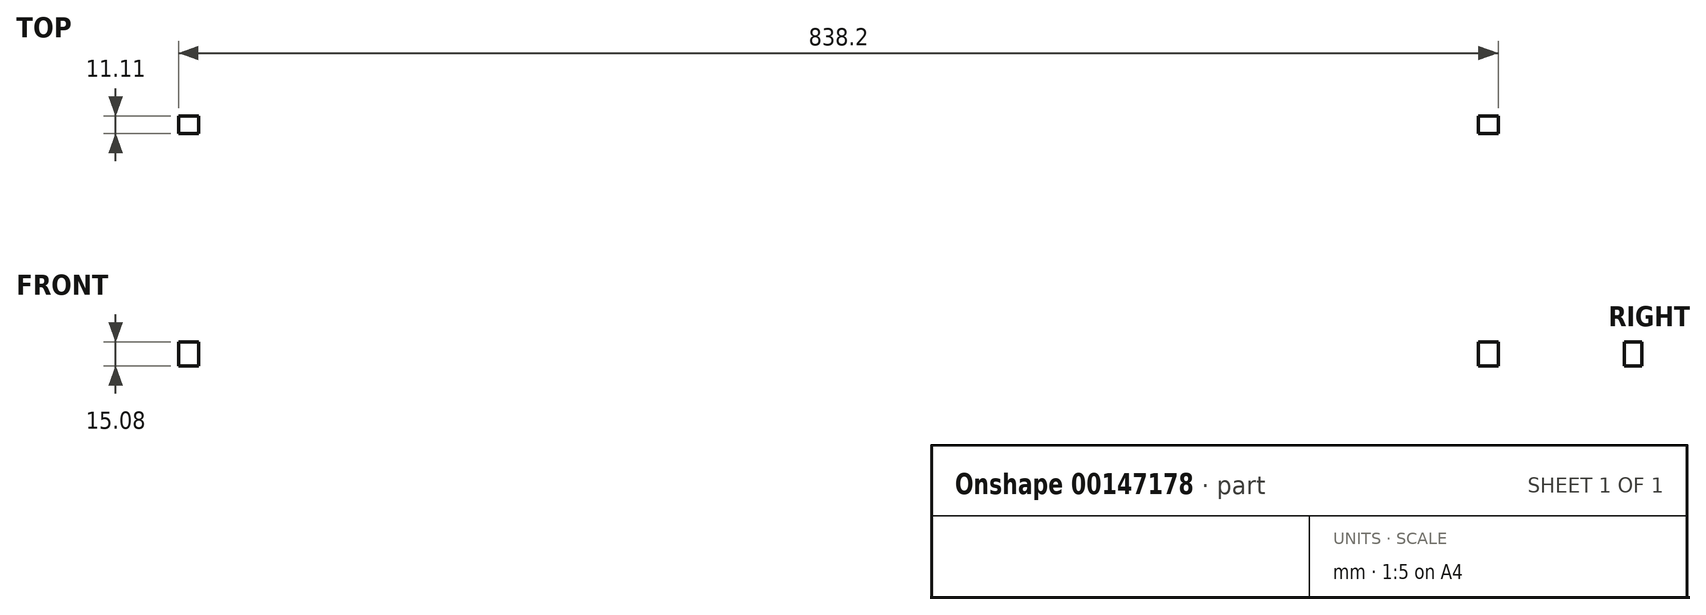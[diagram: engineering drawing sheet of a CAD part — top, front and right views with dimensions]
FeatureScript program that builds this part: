
annotation { "Feature Type Name" : "Feature", "Feature Type Description" : "" }
export const myFeature = defineFeature(function(context is Context, id is Id, definition is map)
    precondition{}
    {
        {
            var Q0;
            Q0=qCreatedBy(makeId("Top.planeOp"),FACE);
            var sketch = newSketch(context, id + "F0", { "sketchPlane" : qUnion([Q0])});
            skLineSegment(sketch, "E0.bottom", {"start": v(0, 0) * mm, "end": v(838.2, 0) * mm});
            skLineSegment(sketch, "E0.top", {"start": v(0, 342.9) * mm, "end": v(838.2, 342.9) * mm});
            skLineSegment(sketch, "E0.left", {"start": v(0, 0) * mm, "end": v(0, 342.9) * mm});
            skLineSegment(sketch, "E0.right", {"start": v(838.2, 0) * mm, "end": v(838.2, 342.9) * mm});
            skLineSegment(sketch, "E1.bottom", {"start": v(0, 0) * mm, "end": v(12.7, 0) * mm});
            skLineSegment(sketch, "E1.top", {"start": v(0, 11.11) * mm, "end": v(12.7, 11.11) * mm});
            skLineSegment(sketch, "E1.left", {"start": v(0, 0) * mm, "end": v(0, 11.11) * mm});
            skLineSegment(sketch, "E1.right", {"start": v(12.7, 0) * mm, "end": v(12.7, 11.11) * mm});
            skLineSegment(sketch, "E2.bottom", {"start": v(12.7, 342.9) * mm, "end": v(0, 342.9) * mm});
            skLineSegment(sketch, "E2.top", {"start": v(12.7, 309.56) * mm, "end": v(0, 309.56) * mm});
            skLineSegment(sketch, "E2.left", {"start": v(12.7, 342.9) * mm, "end": v(12.7, 309.56) * mm});
            skLineSegment(sketch, "E2.right", {"start": v(0, 342.9) * mm, "end": v(0, 309.56) * mm});
            skLineSegment(sketch, "E3.bottom", {"start": v(825.5, 309.56) * mm, "end": v(838.2, 309.56) * mm});
            skLineSegment(sketch, "E3.top", {"start": v(825.5, 342.9) * mm, "end": v(838.2, 342.9) * mm});
            skLineSegment(sketch, "E3.left", {"start": v(825.5, 309.56) * mm, "end": v(825.5, 342.9) * mm});
            skLineSegment(sketch, "E3.right", {"start": v(838.2, 309.56) * mm, "end": v(838.2, 342.9) * mm});
            skLineSegment(sketch, "E4.bottom", {"start": v(838.2, 11.11) * mm, "end": v(825.5, 11.11) * mm});
            skLineSegment(sketch, "E4.top", {"start": v(838.2, 0) * mm, "end": v(825.5, 0) * mm});
            skLineSegment(sketch, "E4.left", {"start": v(838.2, 11.11) * mm, "end": v(838.2, 0) * mm});
            skLineSegment(sketch, "E4.right", {"start": v(825.5, 11.11) * mm, "end": v(825.5, 0) * mm});
            skSolve(sketch);
        }
        {
            var Q0;
            Q0=makeQuery(id+"F0.imprint","IMPRINT",FACE,{"disambiguationData":[TD([[makeQuery(id+"F0.imprint","IMPRINT",EDGE,{"derivedFrom":sQuery(id+"F0.wireOp",EDGE,"E0.bottom")}),1.0]])]});
            extrude(context, id + "F1", {"entities" : qUnion([Q0]), "depth" : 15.08 * mm});
        }
    });
